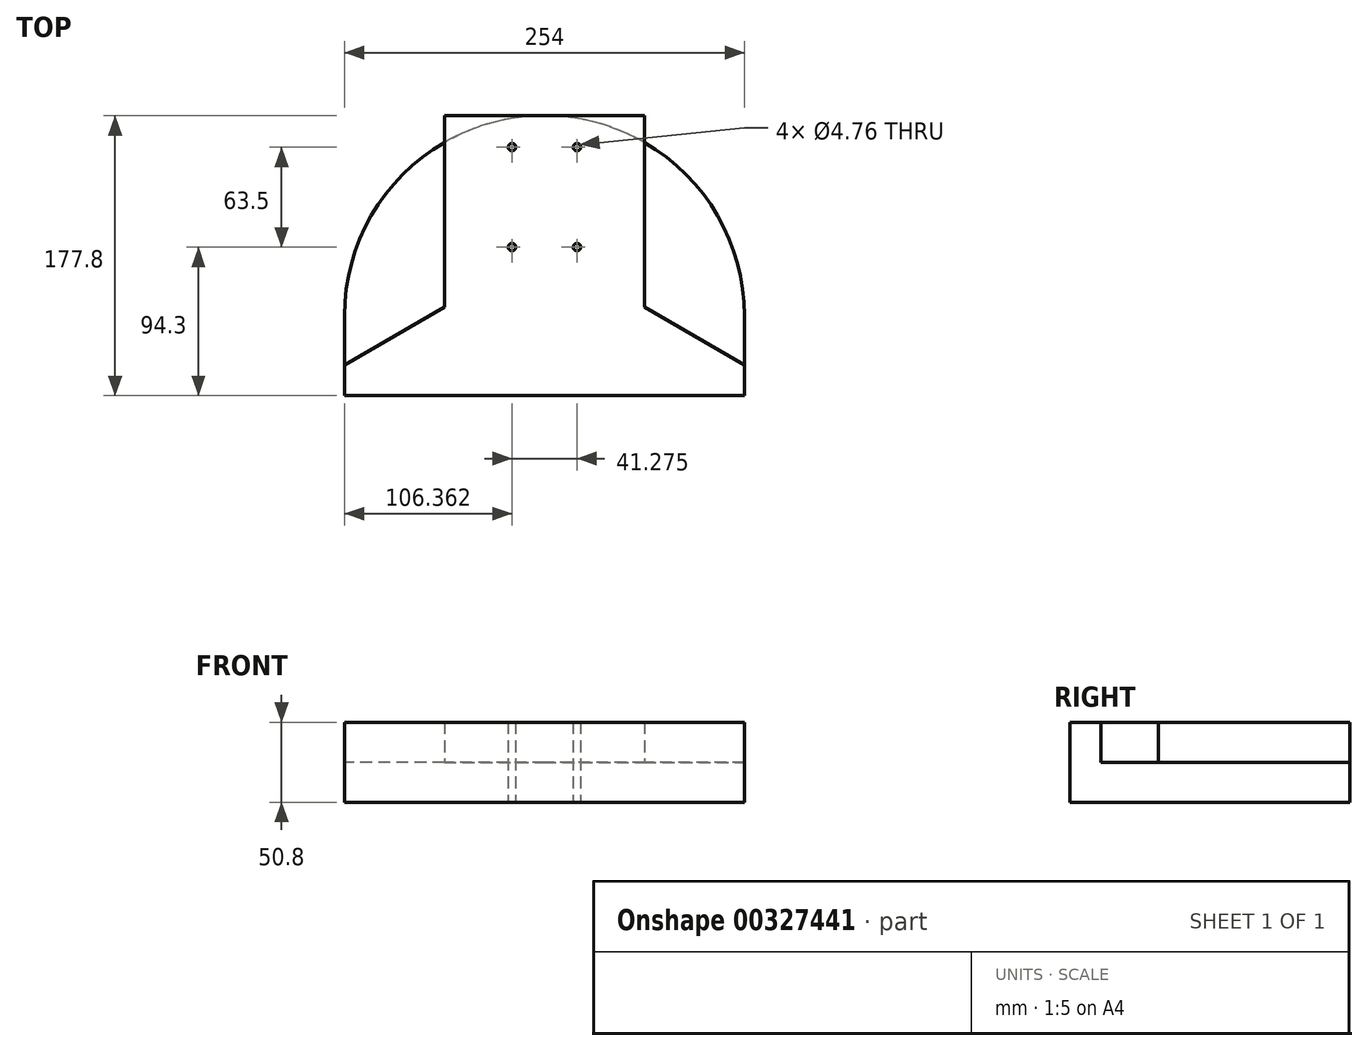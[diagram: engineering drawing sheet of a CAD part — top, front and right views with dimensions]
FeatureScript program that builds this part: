
annotation { "Feature Type Name" : "Feature", "Feature Type Description" : "" }
export const myFeature = defineFeature(function(context is Context, id is Id, definition is map)
    precondition{}
    {
        {
            var Q0;
            Q0=qCreatedBy(makeId("Top.planeOp"),FACE);
            var sketch = newSketch(context, id + "F0", { "sketchPlane" : qUnion([Q0])});
            skLineSegment(sketch, "E0.bottom", {"start": v(0, 0) * mm, "end": v(-127, 0) * mm, "construction": true});
            skLineSegment(sketch, "E0.top", {"start": v(0, 381) * mm, "end": v(-127, 381) * mm, "construction": true});
            skLineSegment(sketch, "E0.left", {"start": v(0, 0) * mm, "end": v(0, 381) * mm, "construction": true});
            skLineSegment(sketch, "E0.right", {"start": v(-127, 0) * mm, "end": v(-127, 381) * mm, "construction": true});
            skLineSegment(sketch, "E1.MirrorCS", {"start": v(0, 381) * mm, "end": v(127, 381) * mm, "construction": true});
            skLineSegment(sketch, "E2.MirrorCS", {"start": v(127, 0) * mm, "end": v(127, 381) * mm, "construction": true});
            skLineSegment(sketch, "E3.MirrorCS", {"start": v(0, 0) * mm, "end": v(127, 0) * mm, "construction": true});
            skLineSegment(sketch, "E4.MirrorCS", {"start": v(-127, 0) * mm, "end": v(-127, -381) * mm, "construction": true});
            skLineSegment(sketch, "E5.MirrorCS", {"start": v(0, 0) * mm, "end": v(0, -381) * mm, "construction": true});
            skLineSegment(sketch, "E6.MirrorCS", {"start": v(127, 0) * mm, "end": v(127, -381) * mm, "construction": true});
            skLineSegment(sketch, "E7.MirrorCS", {"start": v(0, -381) * mm, "end": v(127, -381) * mm, "construction": true});
            skLineSegment(sketch, "E8.MirrorCS", {"start": v(0, -381) * mm, "end": v(-127, -381) * mm, "construction": true});
            skLineSegment(sketch, "E9.bottom", {"start": v(20.64, 361) * mm, "end": v(-20.64, 361) * mm, "construction": true});
            skLineSegment(sketch, "E9.top", {"start": v(20.64, 297.5) * mm, "end": v(-20.64, 297.5) * mm, "construction": true});
            skLineSegment(sketch, "E9.left", {"start": v(20.64, 361) * mm, "end": v(20.64, 297.5) * mm, "construction": true});
            skLineSegment(sketch, "E9.right", {"start": v(-20.64, 361) * mm, "end": v(-20.64, 297.5) * mm, "construction": true});
            skPoint(sketch, "E10", {"position": v(0, 361) * mm});
            skPoint(sketch, "E11", {"position": v(-20.64, 329.25) * mm});
            skPoint(sketch, "E12", {"position": v(20.64, 329.25) * mm});
            skLineSegment(sketch, "E13", {"start": v(-63.5, 381) * mm, "end": v(-63.5, 259.4) * mm});
            skLineSegment(sketch, "E14", {"start": v(-63.5, 259.4) * mm, "end": v(-127, 222.74) * mm});
            skArc(sketch, "E15", {"start": v(0, 381) * mm, "mid": v(-89.8, 343.8) * mm, "end": v(-127, 254) * mm});
            skArc(sketch, "E16.MirrorCS", {"start": v(0, 381) * mm, "mid": v(89.8, 343.8) * mm, "end": v(127, 254) * mm});
            skLineSegment(sketch, "E17", {"start": v(-127, 0) * mm, "end": v(-127, 222.74) * mm});
            skCircle(sketch, "E18", {"center": v(-20.64, 361) * mm, "radius": 2.38 * mm});
            skCircle(sketch, "E19", {"center": v(-20.64, 297.5) * mm, "radius": 2.38 * mm});
            skLineSegment(sketch, "E20", {"start": v(-127, 254) * mm, "end": v(-127, 222.74) * mm});
            skCircle(sketch, "E21.MirrorC", {"center": v(20.64, 297.5) * mm, "radius": 2.38 * mm});
            skCircle(sketch, "E22.MirrorC", {"center": v(20.64, 361) * mm, "radius": 2.38 * mm});
            skLineSegment(sketch, "E23.MirrorCS", {"start": v(127, 0) * mm, "end": v(127, 222.74) * mm});
            skLineSegment(sketch, "E24.MirrorCS", {"start": v(127, 254) * mm, "end": v(127, 222.74) * mm});
            skLineSegment(sketch, "E25.MirrorCS", {"start": v(63.5, 381) * mm, "end": v(63.5, 259.4) * mm});
            skLineSegment(sketch, "E26.MirrorCS", {"start": v(63.5, 259.4) * mm, "end": v(127, 222.74) * mm});
            skCircle(sketch, "E27.MirrorC", {"center": v(20.64, -297.5) * mm, "radius": 2.38 * mm});
            skCircle(sketch, "E28.MirrorC", {"center": v(20.64, -361) * mm, "radius": 2.38 * mm});
            skCircle(sketch, "E29.MirrorC", {"center": v(-20.64, -361) * mm, "radius": 2.38 * mm});
            skCircle(sketch, "E30.MirrorC", {"center": v(-20.64, -297.5) * mm, "radius": 2.38 * mm});
            skLineSegment(sketch, "E31.MirrorCS", {"start": v(20.64, -361) * mm, "end": v(-20.64, -361) * mm, "construction": true});
            skLineSegment(sketch, "E32.MirrorCS", {"start": v(127, 0) * mm, "end": v(127, -222.74) * mm});
            skLineSegment(sketch, "E33.MirrorCS", {"start": v(127, -254) * mm, "end": v(127, -222.74) * mm});
            skLineSegment(sketch, "E34.MirrorCS", {"start": v(20.64, -361) * mm, "end": v(20.64, -297.5) * mm, "construction": true});
            skLineSegment(sketch, "E35.MirrorCS", {"start": v(20.64, -297.5) * mm, "end": v(-20.64, -297.5) * mm, "construction": true});
            skPoint(sketch, "E36.MirrorP", {"position": v(0, -361) * mm});
            skLineSegment(sketch, "E37.MirrorCS", {"start": v(-127, 0) * mm, "end": v(-127, -222.74) * mm});
            skPoint(sketch, "E38.MirrorP", {"position": v(20.64, -329.25) * mm});
            skLineSegment(sketch, "E39.MirrorCS", {"start": v(-127, -254) * mm, "end": v(-127, -222.74) * mm});
            skLineSegment(sketch, "E40.MirrorCS", {"start": v(-63.5, -259.4) * mm, "end": v(-127, -222.74) * mm});
            skArc(sketch, "E41.MirrorCS", {"start": v(0, -381) * mm, "mid": v(89.8, -343.8) * mm, "end": v(127, -254) * mm});
            skLineSegment(sketch, "E42.MirrorCS", {"start": v(-20.64, -361) * mm, "end": v(-20.64, -297.5) * mm, "construction": true});
            skLineSegment(sketch, "E43.MirrorCS", {"start": v(-63.5, -381) * mm, "end": v(-63.5, -259.4) * mm});
            skArc(sketch, "E44.MirrorCS", {"start": v(0, -381) * mm, "mid": v(-89.8, -343.8) * mm, "end": v(-127, -254) * mm});
            skLineSegment(sketch, "E45.MirrorCS", {"start": v(63.5, -259.4) * mm, "end": v(127, -222.74) * mm});
            skLineSegment(sketch, "E46.MirrorCS", {"start": v(63.5, -381) * mm, "end": v(63.5, -259.4) * mm});
            skPoint(sketch, "E47.MirrorP", {"position": v(-20.64, -329.25) * mm});
            skPoint(sketch, "E48", {"position": v(-89.8, 343.8) * mm});
            skLineSegment(sketch, "E49", {"start": v(-40, 361) * mm, "end": v(-40, 297.5) * mm, "construction": true});
            skCircle(sketch, "E50", {"center": v(-40, 329.25) * mm, "radius": 7.5 * mm, "construction": true});
            skLineSegment(sketch, "E51", {"start": v(-127, 203.2) * mm, "end": v(127, 203.2) * mm});
            skLineSegment(sketch, "E52", {"start": v(-63.5, 381) * mm, "end": v(63.5, 381) * mm});
            skSolve(sketch);
        }
        {
            var Q0;
            {var subQ4=sQuery(id+"F0.wireOp",EDGE,"E14");Q0=makeQuery(id+"F0.imprint","IMPRINT",FACE,{"disambiguationData":[TD([[makeQuery(id+"F0.imprint","IMPRINT",EDGE,{"derivedFrom":subQ4}),1.0]])]});}
            var Q1;
            {var subQ0=sQuery(id+"F0.wireOp",EDGE,"E52");var subQ1=sQuery(id+"F0.wireOp",EDGE,"E13");var subQ2=makeQuery(id+"F0.imprint","INTERSECT",VERTEX,{"derivedFrom":[subQ1,subQ0]});Q1=makeQuery(id+"F0.imprint","IMPRINT",FACE,{"disambiguationData":[TD([[makeQuery(id+"F0.imprint","IMPRINT",EDGE,{"disambiguationData":[TD([[subQ2,-1.0]])],"derivedFrom":subQ1}),1.0]])]});}
            var Q2;
            {var subQ0=sQuery(id+"F0.wireOp",EDGE,"E52");var subQ3=sQuery(id+"F0.wireOp",EDGE,"E25.MirrorCS");var subQ5=makeQuery(id+"F0.imprint","INTERSECT",VERTEX,{"derivedFrom":[subQ3,subQ0]});Q2=makeQuery(id+"F0.imprint","IMPRINT",FACE,{"disambiguationData":[TD([[makeQuery(id+"F0.imprint","IMPRINT",EDGE,{"disambiguationData":[TD([[subQ5,-1.0]])],"derivedFrom":subQ3}),-1.0]])]});}
            extrude(context, id + "F1", {"entities" : qUnion([Q0, Q1, Q2]), "depth" : 25.4 * mm, "offsetDistance" : 25.4 * mm});
        }
        {
            var Q0;
            {var subQ0=sQuery(id+"F0.wireOp",EDGE,"E24.MirrorCS");Q0=makeQuery(id+"F0.imprint","IMPRINT",FACE,{"disambiguationData":[TD([[makeQuery(id+"F0.imprint","IMPRINT",EDGE,{"derivedFrom":subQ0}),-1.0]])]});}
            var Q1;
            {var subQ4=sQuery(id+"F0.wireOp",EDGE,"E14");Q1=makeQuery(id+"F0.imprint","IMPRINT",FACE,{"disambiguationData":[TD([[makeQuery(id+"F0.imprint","IMPRINT",EDGE,{"derivedFrom":subQ4}),1.0]])]});}
            var Q2;
            {var subQ0=sQuery(id+"F0.wireOp",EDGE,"E14");Q2=makeQuery(id+"F0.imprint","IMPRINT",FACE,{"disambiguationData":[TD([[makeQuery(id+"F0.imprint","IMPRINT",EDGE,{"derivedFrom":subQ0}),-1.0]])]});}
            extrude(context, id + "F2", {"entities" : qUnion([Q0, Q1, Q2]), "operationType" : NewBodyOperationType.ADD, "oppositeDirection" : true, "depth" : 25.4 * mm, "offsetDistance" : 25.4 * mm});
        }
    });
